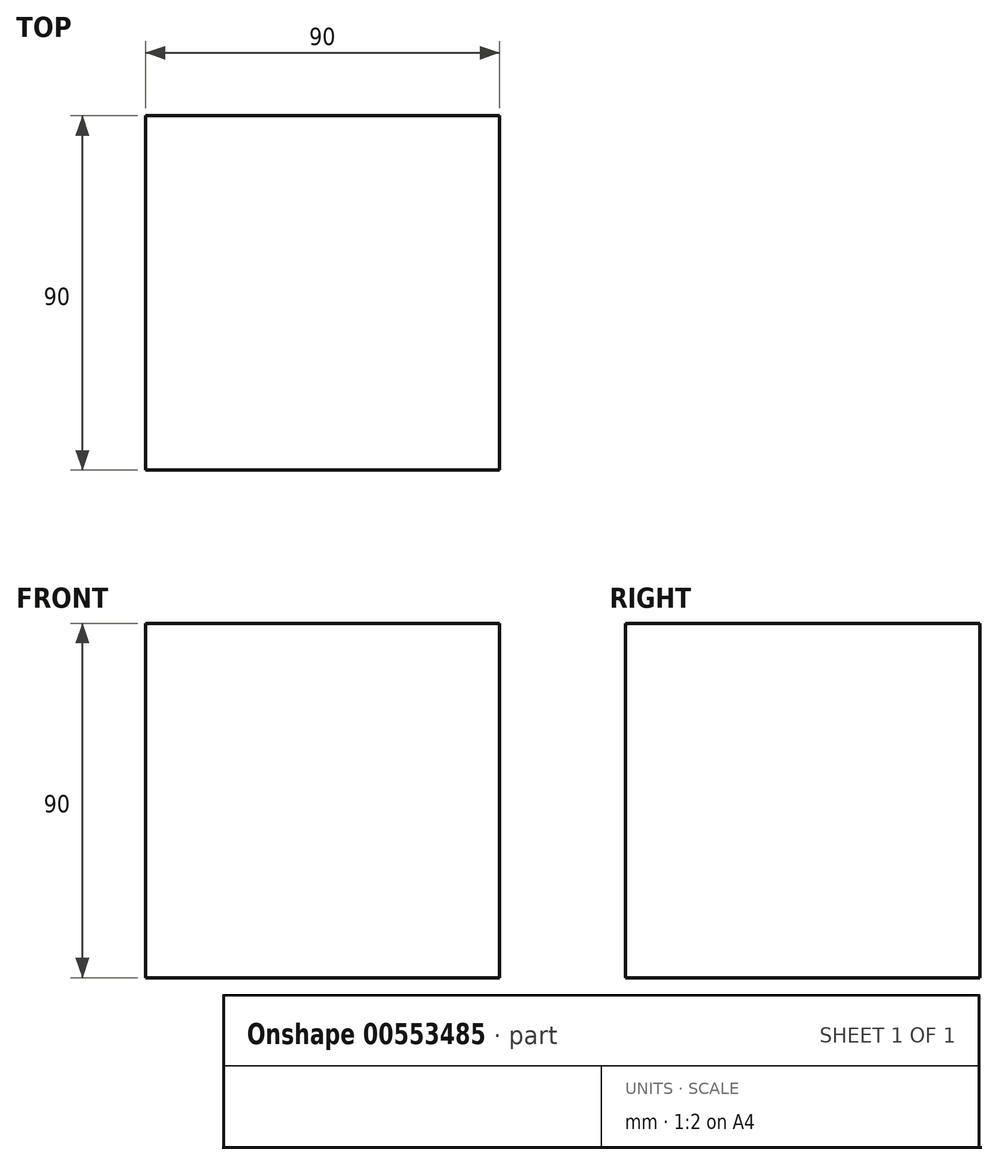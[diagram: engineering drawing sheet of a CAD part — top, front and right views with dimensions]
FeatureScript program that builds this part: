
annotation { "Feature Type Name" : "Feature", "Feature Type Description" : "" }
export const myFeature = defineFeature(function(context is Context, id is Id, definition is map)
    precondition{}
    {
        {
            var Q0;
            Q0=qCreatedBy(makeId("Top.planeOp"),FACE);
            var sketch = newSketch(context, id + "F0", { "sketchPlane" : qUnion([Q0])});
            skLineSegment(sketch, "E0.bottom", {"start": v(45, -45) * mm, "end": v(-45, -45) * mm});
            skLineSegment(sketch, "E0.top", {"start": v(45, 45) * mm, "end": v(-45, 45) * mm});
            skLineSegment(sketch, "E0.left", {"start": v(45, -45) * mm, "end": v(45, 45) * mm});
            skLineSegment(sketch, "E0.right", {"start": v(-45, -45) * mm, "end": v(-45, 45) * mm});
            skPoint(sketch, "E0.middle", {"position": v(0, 0) * mm});
            skSolve(sketch);
        }
        {
            var Q0;
            Q0 = qSketchRegion(id + "F0", true);
            extrude(context, id + "F1", {"entities" : qUnion([Q0]), "endBound" : BoundingType.SYMMETRIC, "depth" : 90 * mm, "offsetDistance" : 25 * mm});
        }
    });
